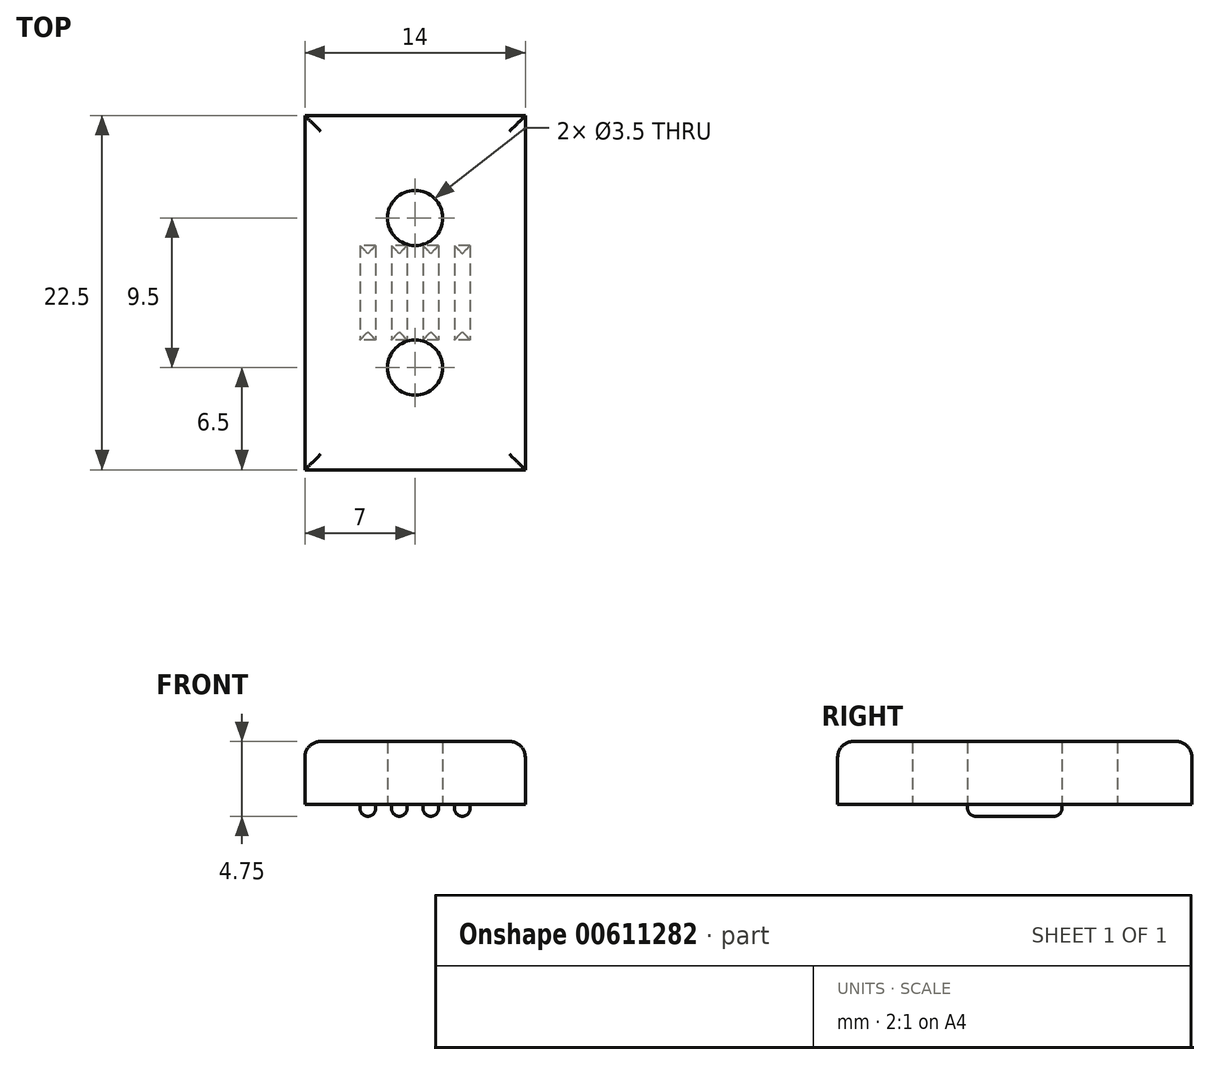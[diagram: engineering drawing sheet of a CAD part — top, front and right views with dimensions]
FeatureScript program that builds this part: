
annotation { "Feature Type Name" : "Feature", "Feature Type Description" : "" }
export const myFeature = defineFeature(function(context is Context, id is Id, definition is map)
    precondition{}
    {
        {
            var Q0;
            Q0=qCreatedBy(makeId("Top.planeOp"),FACE);
            var sketch = newSketch(context, id + "F0", { "sketchPlane" : qUnion([Q0])});
            skLineSegment(sketch, "E0.bottom", {"start": v(0, 0) * mm, "end": v(14, 0) * mm});
            skLineSegment(sketch, "E0.top", {"start": v(0, -22.5) * mm, "end": v(14, -22.5) * mm});
            skLineSegment(sketch, "E0.left", {"start": v(0, 0) * mm, "end": v(0, -22.5) * mm});
            skLineSegment(sketch, "E0.right", {"start": v(14, 0) * mm, "end": v(14, -22.5) * mm});
            skLineSegment(sketch, "E1", {"start": v(0, -6.5) * mm, "end": v(14, -6.5) * mm, "construction": true});
            skLineSegment(sketch, "E2", {"start": v(0, -16) * mm, "end": v(14, -16) * mm, "construction": true});
            skCircle(sketch, "E3", {"center": v(7, -6.5) * mm, "radius": 1.75 * mm});
            skCircle(sketch, "E4", {"center": v(7, -16) * mm, "radius": 1.75 * mm});
            skSolve(sketch);
        }
        {
            var Q0;
            Q0=makeQuery(id+"F0.imprint","IMPRINT",FACE,{"disambiguationData":[TD([[makeQuery(id+"F0.imprint","IMPRINT",EDGE,{"derivedFrom":sQuery(id+"F0.wireOp",EDGE,"E0.bottom")}),-1.0]])]});
            extrude(context, id + "F1", {"entities" : qUnion([Q0]), "depth" : 4 * mm, "offsetDistance" : 25 * mm});
        }
        {
            var Q0;
            Q0=makeQuery(id+"F1.opExtrude","CAP_EDGE",EDGE,{"disambiguationData":[OSD([sQuery(id+"F0.wireOp",EDGE,"E0.bottom")])],"isStart":false});
            var Q1;
            Q1=makeQuery(id+"F1.opExtrude","CAP_EDGE",EDGE,{"disambiguationData":[OSD([sQuery(id+"F0.wireOp",EDGE,"E0.left")])],"isStart":false});
            var Q2;
            Q2=makeQuery(id+"F1.opExtrude","CAP_EDGE",EDGE,{"disambiguationData":[OSD([sQuery(id+"F0.wireOp",EDGE,"E0.right")])],"isStart":false});
            var Q3;
            Q3=makeQuery(id+"F1.opExtrude","CAP_EDGE",EDGE,{"disambiguationData":[OSD([sQuery(id+"F0.wireOp",EDGE,"E0.top")])],"isStart":false});
            fillet(context, id + "F2", {"entities" : qUnion([Q0, Q1, Q2, Q3]), "radius" : 1 * mm, "tangentPropagation" : true, "allowEdgeOverflow" : false});
        }
        {
            var Q0;
            Q0=makeQuery(id+"F1.opExtrude","CAP_FACE",FACE,{"disambiguationData":[OSD([sQuery(id+"F0.wireOp",EDGE,"E0.bottom"),sQuery(id+"F0.wireOp",EDGE,"E0.top"),sQuery(id+"F0.wireOp",EDGE,"E0.left"),sQuery(id+"F0.wireOp",EDGE,"E0.right"),sQuery(id+"F0.wireOp",EDGE,"E3"),sQuery(id+"F0.wireOp",EDGE,"E4")])],"isStart":true});
            var sketch = newSketch(context, id + "F3", { "sketchPlane" : qUnion([Q0])});
            skLineSegment(sketch, "E5.bottom", {"start": v(14, 8.25) * mm, "end": v(0, 8.25) * mm, "construction": true});
            skLineSegment(sketch, "E5.top", {"start": v(14, 14.25) * mm, "end": v(0, 14.25) * mm, "construction": true});
            skLineSegment(sketch, "E5.left", {"start": v(14, 8.25) * mm, "end": v(14, 14.25) * mm, "construction": true});
            skLineSegment(sketch, "E5.right", {"start": v(0, 8.25) * mm, "end": v(0, 14.25) * mm, "construction": true});
            skLineSegment(sketch, "E6.bottom", {"start": v(10.5, 8.25) * mm, "end": v(9.5, 8.25) * mm});
            skLineSegment(sketch, "E6.top", {"start": v(10.5, 14.25) * mm, "end": v(9.5, 14.25) * mm});
            skLineSegment(sketch, "E6.left", {"start": v(10.5, 8.25) * mm, "end": v(10.5, 14.25) * mm});
            skLineSegment(sketch, "E6.right", {"start": v(9.5, 8.25) * mm, "end": v(9.5, 14.25) * mm});
            skLineSegment(sketch, "E7.bottom", {"start": v(8.5, 8.25) * mm, "end": v(7.5, 8.25) * mm});
            skLineSegment(sketch, "E7.top", {"start": v(8.5, 14.25) * mm, "end": v(7.5, 14.25) * mm});
            skLineSegment(sketch, "E7.left", {"start": v(8.5, 8.25) * mm, "end": v(8.5, 14.25) * mm});
            skLineSegment(sketch, "E7.right", {"start": v(7.5, 8.25) * mm, "end": v(7.5, 14.25) * mm});
            skLineSegment(sketch, "E8.bottom", {"start": v(6.5, 8.25) * mm, "end": v(5.5, 8.25) * mm});
            skLineSegment(sketch, "E8.top", {"start": v(6.5, 14.25) * mm, "end": v(5.5, 14.25) * mm});
            skLineSegment(sketch, "E8.left", {"start": v(6.5, 8.25) * mm, "end": v(6.5, 14.25) * mm});
            skLineSegment(sketch, "E8.right", {"start": v(5.5, 8.25) * mm, "end": v(5.5, 14.25) * mm});
            skLineSegment(sketch, "E9.bottom", {"start": v(4.5, 8.25) * mm, "end": v(3.5, 8.25) * mm});
            skLineSegment(sketch, "E9.top", {"start": v(4.5, 14.25) * mm, "end": v(3.5, 14.25) * mm});
            skLineSegment(sketch, "E9.left", {"start": v(4.5, 8.25) * mm, "end": v(4.5, 14.25) * mm});
            skLineSegment(sketch, "E9.right", {"start": v(3.5, 8.25) * mm, "end": v(3.5, 14.25) * mm});
            skSolve(sketch);
        }
        {
            var Q0;
            Q0=makeQuery(id+"F3.imprint","IMPRINT",FACE,{"disambiguationData":[TD([[makeQuery(id+"F3.imprint","IMPRINT",EDGE,{"derivedFrom":sQuery(id+"F3.wireOp",EDGE,"E9.bottom")}),-1.0]])]});
            var Q1;
            Q1=makeQuery(id+"F3.imprint","IMPRINT",FACE,{"disambiguationData":[TD([[makeQuery(id+"F3.imprint","IMPRINT",EDGE,{"derivedFrom":sQuery(id+"F3.wireOp",EDGE,"E8.bottom")}),-1.0]])]});
            var Q2;
            Q2=makeQuery(id+"F3.imprint","IMPRINT",FACE,{"disambiguationData":[TD([[makeQuery(id+"F3.imprint","IMPRINT",EDGE,{"derivedFrom":sQuery(id+"F3.wireOp",EDGE,"E7.bottom")}),-1.0]])]});
            var Q3;
            Q3=makeQuery(id+"F3.imprint","IMPRINT",FACE,{"disambiguationData":[TD([[makeQuery(id+"F3.imprint","IMPRINT",EDGE,{"derivedFrom":sQuery(id+"F3.wireOp",EDGE,"E6.bottom")}),-1.0]])]});
            extrude(context, id + "F4", {"entities" : qUnion([Q0, Q1, Q2, Q3]), "operationType" : NewBodyOperationType.ADD, "depth" : .75 * mm, "offsetDistance" : 25 * mm});
        }
        {
            var Q0;
            Q0=makeQuery(id+"F4.opExtrude","CAP_FACE",FACE,{"disambiguationData":[OSD([sQuery(id+"F3.wireOp",EDGE,"E6.bottom"),sQuery(id+"F3.wireOp",EDGE,"E6.top"),sQuery(id+"F3.wireOp",EDGE,"E6.left"),sQuery(id+"F3.wireOp",EDGE,"E6.right")])],"isStart":false});
            var Q1;
            Q1=makeQuery(id+"F4.opExtrude","CAP_FACE",FACE,{"disambiguationData":[OSD([sQuery(id+"F3.wireOp",EDGE,"E7.bottom"),sQuery(id+"F3.wireOp",EDGE,"E7.top"),sQuery(id+"F3.wireOp",EDGE,"E7.left"),sQuery(id+"F3.wireOp",EDGE,"E7.right")])],"isStart":false});
            var Q2;
            Q2=makeQuery(id+"F4.opExtrude","CAP_FACE",FACE,{"disambiguationData":[OSD([sQuery(id+"F3.wireOp",EDGE,"E8.bottom"),sQuery(id+"F3.wireOp",EDGE,"E8.top"),sQuery(id+"F3.wireOp",EDGE,"E8.left"),sQuery(id+"F3.wireOp",EDGE,"E8.right")])],"isStart":false});
            var Q3;
            Q3=makeQuery(id+"F4.opExtrude","CAP_FACE",FACE,{"disambiguationData":[OSD([sQuery(id+"F3.wireOp",EDGE,"E9.bottom"),sQuery(id+"F3.wireOp",EDGE,"E9.top"),sQuery(id+"F3.wireOp",EDGE,"E9.left"),sQuery(id+"F3.wireOp",EDGE,"E9.right")])],"isStart":false});
            fillet(context, id + "F5", {"entities" : qUnion([Q0, Q1, Q2, Q3]), "radius" : .5 * mm, "tangentPropagation" : true, "allowEdgeOverflow" : false});
        }
    });
